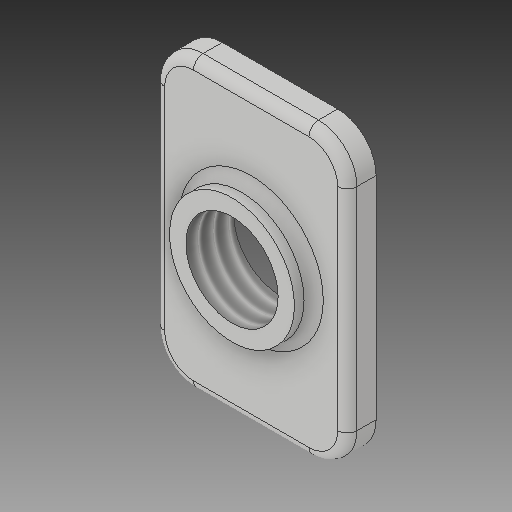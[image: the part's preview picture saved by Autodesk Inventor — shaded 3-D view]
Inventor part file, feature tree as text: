
AUTODESK INVENTOR PART (.ipt)
format: ipt  version: 2018 (Build 220112000, 112)  size: 164,864 bytes
history: native  units: mm
features: other x3, sketch x2
ambient origin geometry x8: Origin, YZ Plane, XZ Plane, XY Plane, X Axis, Y Axis, Z Axis, Center Point
bodies: Solid1 (feature_tree)
feature tree (5):
  other  "M5 Tee Nut_MIR_MIR_MIR_MIR_MIR.ipt"
  other  "Solid1::M5 Tee Nut_MIR_MIR_MIR_MIR_MIR.ipt"
  other  "TaggingFeature1"
  sketch  "Sketch1"  dims[d0=10.0mm]
  sketch  "Sketch2"
